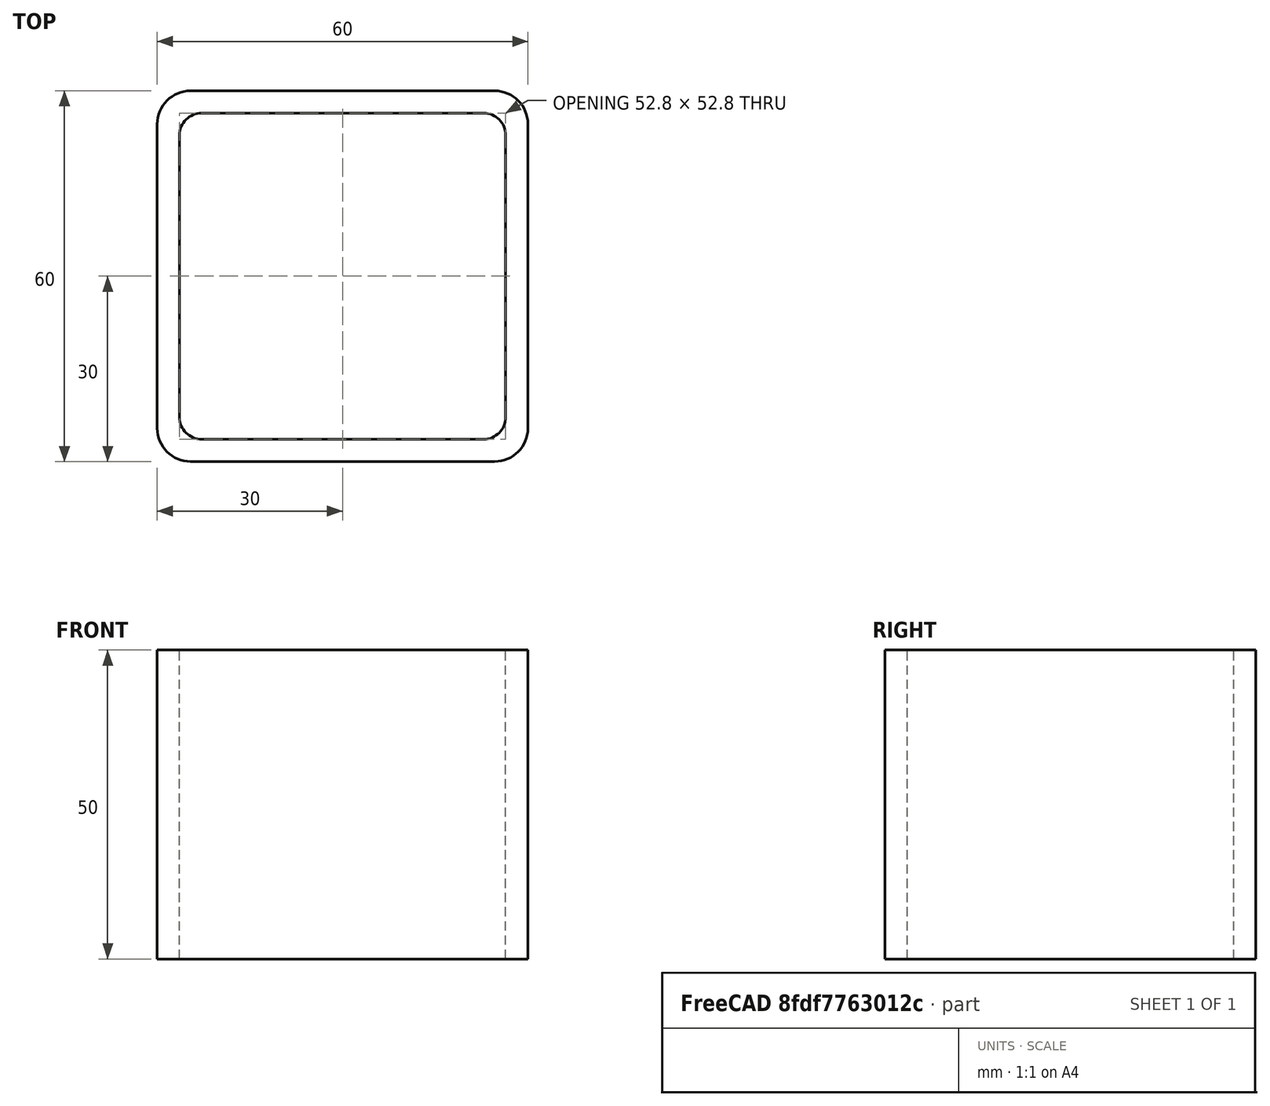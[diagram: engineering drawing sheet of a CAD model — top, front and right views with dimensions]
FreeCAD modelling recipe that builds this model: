
FCSTD DOCUMENT  (FreeCAD 0.15R4671 (Git))
Label: Square hollow section 60x60x3.6 EN10219 S235JRH
License: All rights reserved
LicenseURL: http://en.wikipedia.org/wiki/All_rights_reserved
objects: Sketcher::SketchObject×1, Part::Extrusion×1
note: 2 computed .brp shape members not serialized (recipe doc carries the construction recipe); baked Part::Feature solids carry a one-line shape summary decoded from their .brp

FEATURE [Sketcher::SketchObject] Sketch
  sketch-geometry (16):
    g0: LineSegment StartX=-22.8 StartY=26.4 StartZ=0 EndX=22.8 EndY=26.4 EndZ=0
    g1: LineSegment StartX=26.4 StartY=22.8 StartZ=0 EndX=26.4 EndY=-22.8 EndZ=0
    g2: LineSegment StartX=22.8 StartY=-26.4 StartZ=0 EndX=-22.8 EndY=-26.4 EndZ=0
    g3: LineSegment StartX=-26.4 StartY=-22.8 StartZ=0 EndX=-26.4 EndY=22.8 EndZ=0
    g4: LineSegment StartX=-24.6 StartY=30 StartZ=0 EndX=24.6 EndY=30 EndZ=0
    g5: LineSegment StartX=30 StartY=24.6 StartZ=0 EndX=30 EndY=-24.6 EndZ=0
    g6: LineSegment StartX=24.6 StartY=-30 StartZ=0 EndX=-24.6 EndY=-30 EndZ=0
    g7: LineSegment StartX=-30 StartY=-24.6 StartZ=0 EndX=-30 EndY=24.6 EndZ=0
    g8: ArcOfCircle CenterX=-22.8 CenterY=22.8 CenterZ=0 NormalX=0 NormalY=0 NormalZ=1 Radius=3.6 StartAngle=1.5708 EndAngle=3.14159
    g9: ArcOfCircle CenterX=22.8 CenterY=22.8 CenterZ=0 NormalX=0 NormalY=0 NormalZ=1 Radius=3.6 StartAngle=0 EndAngle=1.5708
    g10: ArcOfCircle CenterX=22.8 CenterY=-22.8 CenterZ=0 NormalX=0 NormalY=0 NormalZ=1 Radius=3.6 StartAngle=4.71239 EndAngle=6.28319
    g11: ArcOfCircle CenterX=-22.8 CenterY=-22.8 CenterZ=0 NormalX=0 NormalY=0 NormalZ=1 Radius=3.6 StartAngle=3.14159 EndAngle=4.71239
    g12: ArcOfCircle CenterX=24.6 CenterY=24.6 CenterZ=0 NormalX=0 NormalY=0 NormalZ=1 Radius=5.4 StartAngle=0 EndAngle=1.5708
    g13: ArcOfCircle CenterX=24.6 CenterY=-24.6 CenterZ=0 NormalX=0 NormalY=0 NormalZ=1 Radius=5.4 StartAngle=4.71239 EndAngle=6.28319
    g14: ArcOfCircle CenterX=-24.6 CenterY=-24.6 CenterZ=0 NormalX=0 NormalY=0 NormalZ=1 Radius=5.4 StartAngle=3.14159 EndAngle=4.71239
    g15: ArcOfCircle CenterX=-24.6 CenterY=24.6 CenterZ=0 NormalX=0 NormalY=0 NormalZ=1 Radius=5.4 StartAngle=1.5708 EndAngle=3.14159
  constraints (36):
    c: Horizontal(g2)
    c: Vertical(g3)
    c: Horizontal(g6)
    c: Vertical(g7)
    c: Tangent(g3,g8) = 1.5708
    c: Tangent(g0,g8) = 1.5708
    c: Tangent(g0,g9) = 1.5708
    c: Tangent(g1,g9) = 1.5708
    c: Tangent(g1,g10) = 1.5708
    c: Tangent(g2,g10) = 1.5708
    c: Tangent(g2,g11) = 1.5708
    c: Tangent(g3,g11) = 1.5708
    c: Tangent(g4,g12) = 1.5708
    c: Tangent(g5,g12) = 1.5708
    c: Tangent(g5,g13) = 1.5708
    c: Tangent(g6,g13) = 1.5708
    c: Tangent(g6,g14) = 1.5708
    c: Tangent(g7,g14) = 1.5708
    c: Tangent(g7,g15) = 1.5708
    c: Tangent(g4,g15) = 1.5708
    c: Equal(g9,g8)
    c: Equal(g9,g11)
    c: Equal(g9,g10)
    c: Equal(g12,g15)
    c: Equal(g12,g14)
    c: Equal(g12,g13)
    c: Symmetric(g4,g6,g-1)
    c: Symmetric(g7,g5,g-2)
    c: DistanceY(g4,g6) = -60
    c: DistanceX(g7,g5) = 60
    c: Symmetric(g3,g1,g-2)
    c: Symmetric(g0,g2,g-1)
    c: DistanceY(g0,g4) = 3.6
    c: DistanceX(g5,g1) = -3.6
    c: Radius(g9) = 3.6
    c: Radius(g12) = 5.4
FEATURE [Part::Extrusion] Extrude  label="Square hollow section 60x60x3.6 EN10219 S235JRH"
  Base = -> Sketch
  Dir = (0,0,50)
  Solid = true
